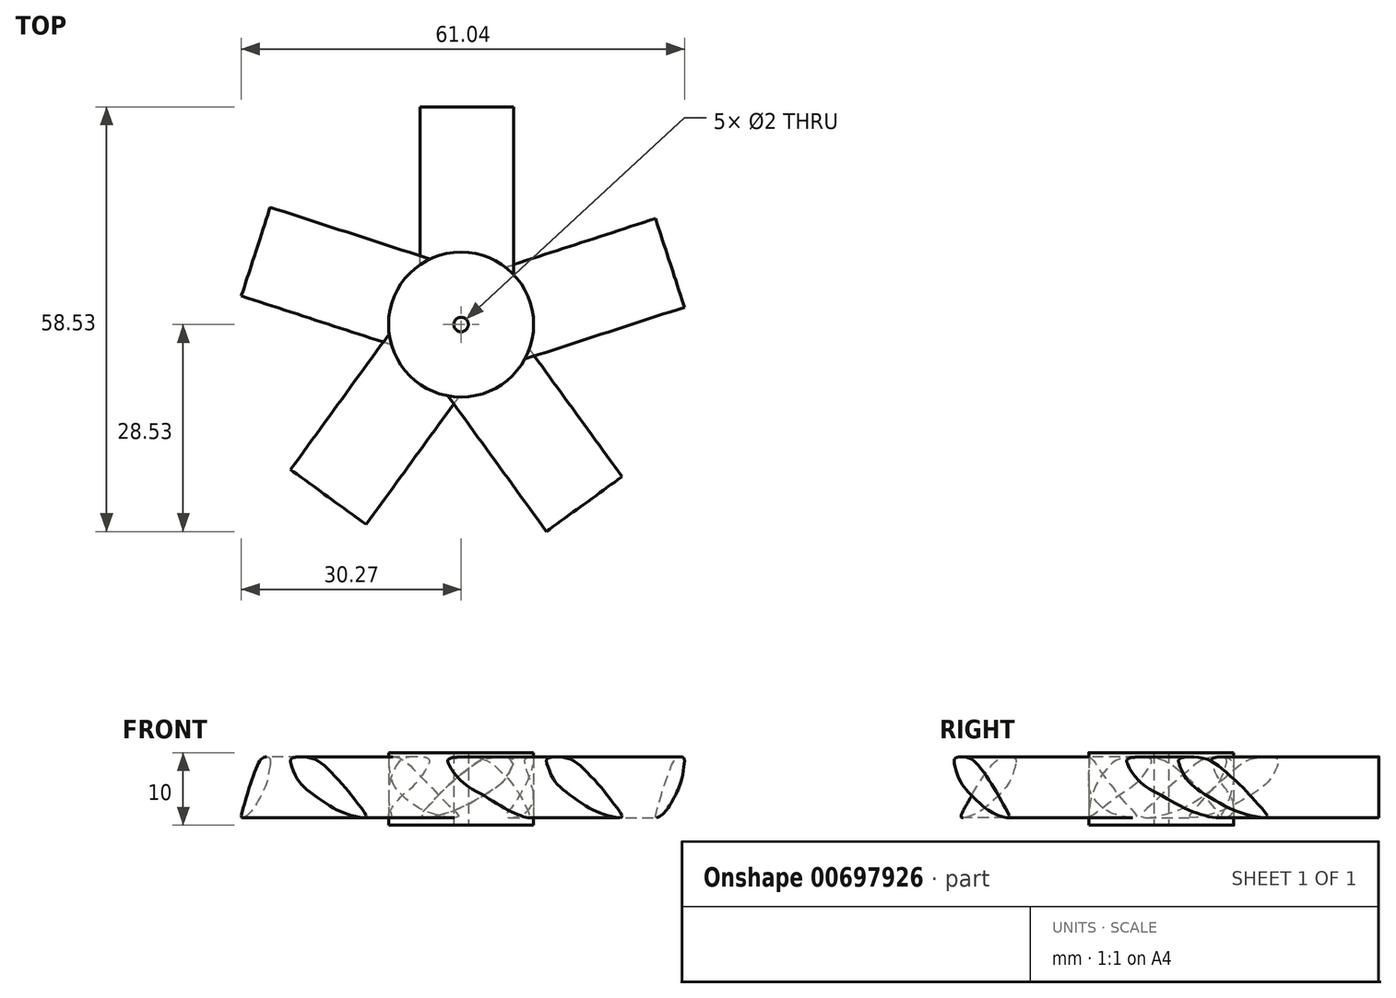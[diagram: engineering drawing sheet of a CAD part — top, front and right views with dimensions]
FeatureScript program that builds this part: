
annotation { "Feature Type Name" : "Feature", "Feature Type Description" : "" }
export const myFeature = defineFeature(function(context is Context, id is Id, definition is map)
    precondition{}
    {
        {
            var Q0;
            Q0=qCreatedBy(makeId("Top.planeOp"),FACE);
            var sketch = newSketch(context, id + "F0", { "sketchPlane" : qUnion([Q0])});
            skCircle(sketch, "E0", {"center": v(0, 0) * mm, "radius": 10 * mm});
            skCircle(sketch, "E1", {"center": v(0, 0) * mm, "radius": 1 * mm});
            skSolve(sketch);
        }
        {
            var Q0;
            Q0=makeQuery(id+"F0.imprint","IMPRINT",FACE,{"disambiguationData":[TD([[makeQuery(id+"F0.imprint","IMPRINT",EDGE,{"derivedFrom":sQuery(id+"F0.wireOp",EDGE,"E0")}),1.0]])]});
            extrude(context, id + "F1", {"entities" : qUnion([Q0]), "depth" : 10 * mm, "offsetDistance" : 25 * mm});
        }
        {
            var Q0;
            Q0=qCreatedBy(makeId("Right.planeOp"),FACE);
            var sketch = newSketch(context, id + "F2", { "sketchPlane" : qUnion([Q0])});
            skLineSegment(sketch, "E2", {"start": v(0, 47.9) * mm, "end": v(0, -34.49) * mm});
            skSolve(sketch);
        }
        {
            var Q0;
            Q0=qCreatedBy(makeId("Front.planeOp"),FACE);
            cPlane(context, id + "F3", {"entities" : qUnion([Q0]), "cplaneType" : CPlaneType.OFFSET, "offset" : 10 * mm, "oppositeDirection" : true, "width" : 150 * mm, "height" : 150 * mm});
        }
        {
            var Q0;
            Q0=qCreatedBy(id+"F3.planeOp",FACE);
            var sketch = newSketch(context, id + "F4", { "sketchPlane" : qUnion([Q0])});
            skFitSpline(sketch, "E3", {"points": [v(7.17, 8.46) * mm, v(5.93, 6.2) * mm, v(3.94, 4.61) * mm, v(0, 2.42) * mm, v(-3.03, 1.39) * mm, v(-5.6, 1.18) * mm, v(-4.16, 3) * mm, v(-2.51, 4.78) * mm, v(0.58, 7.5) * mm, v(2.91, 9) * mm, v(5.52, 9.42) * mm, v(7.14, 9.14) * mm, v(7.17, 8.46) * mm]});
            skSolve(sketch);
        }
        {
            var Q0;
            Q0=makeQuery(id+"F4.imprint","IMPRINT",FACE,{"disambiguationData":[TD([[makeQuery(id+"F4.imprint","IMPRINT",EDGE,{"derivedFrom":sQuery(id+"F4.wireOp",EDGE,"E3")}),-1.0]])]});
            extrude(context, id + "F5", {"entities" : qUnion([Q0]), "operationType" : NewBodyOperationType.ADD, "depth" : 5 * mm, "offsetDistance" : 25 * mm});
        }
        {
            var Q0;
            Q0=makeQuery(id+"F5.opExtrude","CAP_FACE",FACE,{"disambiguationData":[OSD([sQuery(id+"F4.wireOp",EDGE,"E3")])],"isStart":true});
            extrude(context, id + "F6", {"entities" : qUnion([Q0]), "operationType" : NewBodyOperationType.ADD, "depth" : 20 * mm, "offsetDistance" : 25 * mm});
        }
        {
            var Q0;
            Q0=makeQuery(id+"F1.opExtrude","SWEPT_BODY",BODY,{"disambiguationData":[OSD([sQuery(id+"F0.wireOp",EDGE,"E0"),sQuery(id+"F0.wireOp",EDGE,"E1")])]});
            var Q1;
            Q1=sQuery(id+"F2.wireOp",EDGE,"E2");
            circularPattern(context, id + "F7", {"entities" : qUnion([Q0]), "axis" : qUnion([Q1]), "angle" : 360 * degree, "instanceCount" : 5, "equalSpace" : true});
        }
    });
